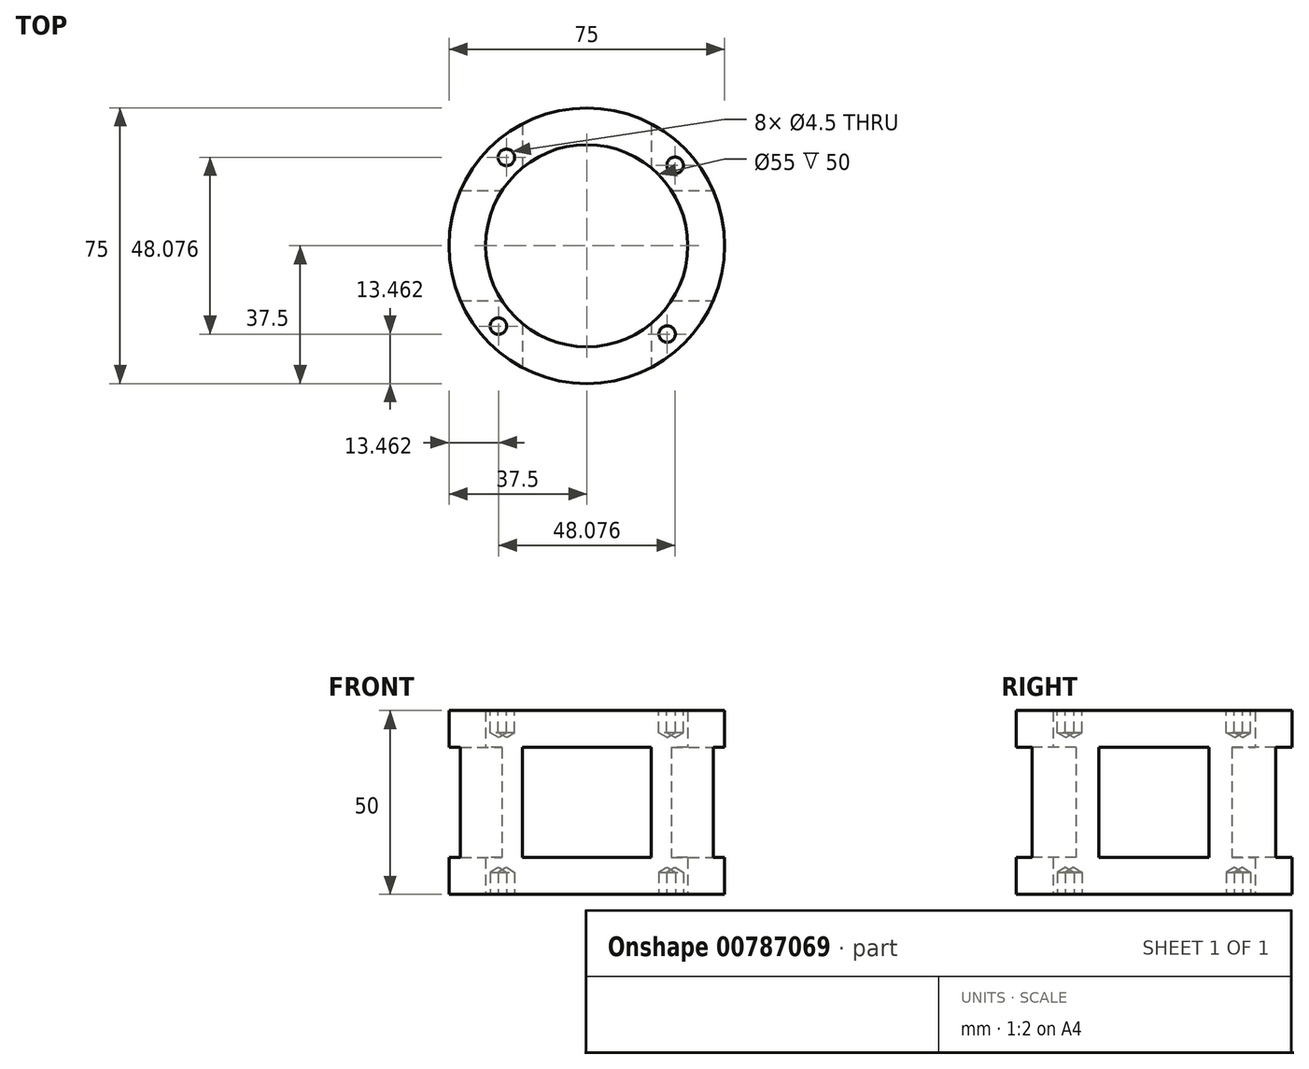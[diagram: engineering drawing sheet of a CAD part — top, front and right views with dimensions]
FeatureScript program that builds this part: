
annotation { "Feature Type Name" : "Feature", "Feature Type Description" : "" }
export const myFeature = defineFeature(function(context is Context, id is Id, definition is map)
    precondition{}
    {
        {
            var Q0;
            Q0=qCreatedBy(makeId("Top.planeOp"),FACE);
            var sketch = newSketch(context, id + "F0", { "sketchPlane" : qUnion([Q0])});
            skCircle(sketch, "E0", {"center": v(0, 0) * mm, "radius": 27.5 * mm});
            skCircle(sketch, "E1", {"center": v(0, 0) * mm, "radius": 37.5 * mm});
            skSolve(sketch);
        }
        {
            assignVariable(context, id + "F1", {"variableType" : VariableType.LENGTH, "name" : "hauteur", "lengthValue" : 50 * mm});
        }
        {
            var Q0;
            Q0=makeQuery(id+"F0.imprint","IMPRINT",FACE,{"disambiguationData":[TD([[makeQuery(id+"F0.imprint","IMPRINT",EDGE,{"derivedFrom":sQuery(id+"F0.wireOp",EDGE,"E0")}),-1.0]])]});
            extrude(context, id + "F2", {"entities" : qUnion([Q0]), "depth" : getVariable(context, 'hauteur'), "offsetDistance" : 25 * mm});
        }
        {
            var Q0;
            Q0=qCreatedBy(makeId("Front.planeOp"),FACE);
            var sketch = newSketch(context, id + "F3", { "sketchPlane" : qUnion([Q0])});
            skLineSegment(sketch, "E2.bottom", {"start": v(-17.5, 40) * mm, "end": v(17.5, 40) * mm});
            skLineSegment(sketch, "E2.top", {"start": v(-17.5, 10) * mm, "end": v(17.5, 10) * mm});
            skLineSegment(sketch, "E2.left", {"start": v(-17.5, 40) * mm, "end": v(-17.5, 10) * mm});
            skLineSegment(sketch, "E2.right", {"start": v(17.5, 40) * mm, "end": v(17.5, 10) * mm});
            skPoint(sketch, "E2.middle", {"position": v(0, 25) * mm});
            skSolve(sketch);
        }
        {
            var Q0;
            Q0 = qSketchRegion(id + "F3", true);
            extrude(context, id + "F4", {"entities" : qUnion([Q0]), "operationType" : NewBodyOperationType.REMOVE, "endBound" : BoundingType.THROUGH_ALL, "oppositeDirection" : true, "depth" : 25 * mm, "offsetDistance" : 25 * mm, "hasSecondDirection" : true, "secondDirectionBound" : BoundingType.THROUGH_ALL, "secondDirectionOppositeDirection" : false, "secondDirectionDepth" : 25 * mm});
        }
        {
            var Q0;
            Q0=qCreatedBy(makeId("Right.planeOp"),FACE);
            var sketch = newSketch(context, id + "F5", { "sketchPlane" : qUnion([Q0])});
            skLineSegment(sketch, "E3.bottom", {"start": v(15, 40) * mm, "end": v(-15, 40) * mm});
            skLineSegment(sketch, "E3.top", {"start": v(15, 10) * mm, "end": v(-15, 10) * mm});
            skLineSegment(sketch, "E3.left", {"start": v(15, 40) * mm, "end": v(15, 10) * mm});
            skLineSegment(sketch, "E3.right", {"start": v(-15, 40) * mm, "end": v(-15, 10) * mm});
            skPoint(sketch, "E3.middle", {"position": v(0, 25) * mm});
            skSolve(sketch);
        }
        {
            var Q0;
            Q0 = qSketchRegion(id + "F5", true);
            extrude(context, id + "F6", {"entities" : qUnion([Q0]), "operationType" : NewBodyOperationType.REMOVE, "endBound" : BoundingType.THROUGH_ALL, "oppositeDirection" : true, "depth" : 25 * mm, "offsetDistance" : 25 * mm, "hasSecondDirection" : true, "secondDirectionBound" : BoundingType.THROUGH_ALL, "secondDirectionOppositeDirection" : false, "secondDirectionDepth" : 25 * mm});
        }
        {
            var Q0;
            Q0=makeQuery(id+"F2.opExtrude","CAP_FACE",FACE,{"disambiguationData":[OSD([sQuery(id+"F0.wireOp",EDGE,"E0"),sQuery(id+"F0.wireOp",EDGE,"E1")])],"isStart":false});
            var sketch = newSketch(context, id + "F7", { "sketchPlane" : qUnion([Q0])});
            skPoint(sketch, "E4", {"position": v(21.87, -24.04) * mm});
            skPoint(sketch, "E5.1.0", {"position": v(24.04, 21.87) * mm});
            skPoint(sketch, "E5.2.0", {"position": v(-21.87, 24.04) * mm});
            skPoint(sketch, "E5.3.0", {"position": v(-24.04, -21.87) * mm});
            skPoint(sketch, "E5.center", {"position": v(0, 0) * mm});
            skSolve(sketch);
        }
        {
            var Q0;
            Q0=sQuery(id+"F7.wireOp",VERTEX,"E4");
            var Q1;
            Q1=sQuery(id+"F7.wireOp",VERTEX,"E5.1.0");
            var Q2;
            Q2=sQuery(id+"F7.wireOp",VERTEX,"E5.2.0");
            var Q3;
            Q3=sQuery(id+"F7.wireOp",VERTEX,"E5.3.0");
            var Q4;
            Q4=makeQuery(id+"F2.opExtrude","SWEPT_BODY",BODY,{"disambiguationData":[OSD([sQuery(id+"F0.wireOp",EDGE,"E0"),sQuery(id+"F0.wireOp",EDGE,"E1")])]});
            hole(context, id + "F8", {"style" : HoleStyle.SIMPLE, "endStyle" : HoleEndStyle.BLIND, "holeDiameter" : 4.5 * mm, "majorDiameter" : 5 * mm, "holeDepth" : 6 * mm, "isTappedThrough" : true, "tappedDepth" : 12 * mm, "tapClearance" : 3, "locations" : qUnion([Q0, Q1, Q2, Q3]), "scope" : qUnion([Q4])});
        }
        {
            var Q0;
            Q0=makeQuery(id+"F2.opExtrude","CAP_FACE",FACE,{"disambiguationData":[OSD([sQuery(id+"F0.wireOp",EDGE,"E0"),sQuery(id+"F0.wireOp",EDGE,"E1")])],"isStart":true});
            var sketch = newSketch(context, id + "F9", { "sketchPlane" : qUnion([Q0])});
            skPoint(sketch, "E6", {"position": v(-24.04, 21.87) * mm});
            skPoint(sketch, "E7.1.0", {"position": v(-21.87, -24.04) * mm});
            skPoint(sketch, "E7.2.0", {"position": v(24.04, -21.87) * mm});
            skPoint(sketch, "E7.3.0", {"position": v(21.87, 24.04) * mm});
            skPoint(sketch, "E7.center", {"position": v(0, 0) * mm});
            skSolve(sketch);
        }
        {
            var Q0;
            Q0=sQuery(id+"F9.wireOp",VERTEX,"E7.3.0");
            var Q1;
            Q1=sQuery(id+"F9.wireOp",VERTEX,"E7.2.0");
            var Q2;
            Q2=sQuery(id+"F9.wireOp",VERTEX,"E6");
            var Q3;
            Q3=sQuery(id+"F9.wireOp",VERTEX,"E7.1.0");
            var Q4;
            Q4=makeQuery(id+"F2.opExtrude","SWEPT_BODY",BODY,{"disambiguationData":[OSD([sQuery(id+"F0.wireOp",EDGE,"E0"),sQuery(id+"F0.wireOp",EDGE,"E1")])]});
            hole(context, id + "F10", {"style" : HoleStyle.SIMPLE, "endStyle" : HoleEndStyle.BLIND, "holeDiameter" : 4.5 * mm, "majorDiameter" : 5 * mm, "holeDepth" : 6 * mm, "isTappedThrough" : true, "tappedDepth" : 12 * mm, "tapClearance" : 3, "locations" : qUnion([Q0, Q1, Q2, Q3]), "scope" : qUnion([Q4])});
        }
    });
